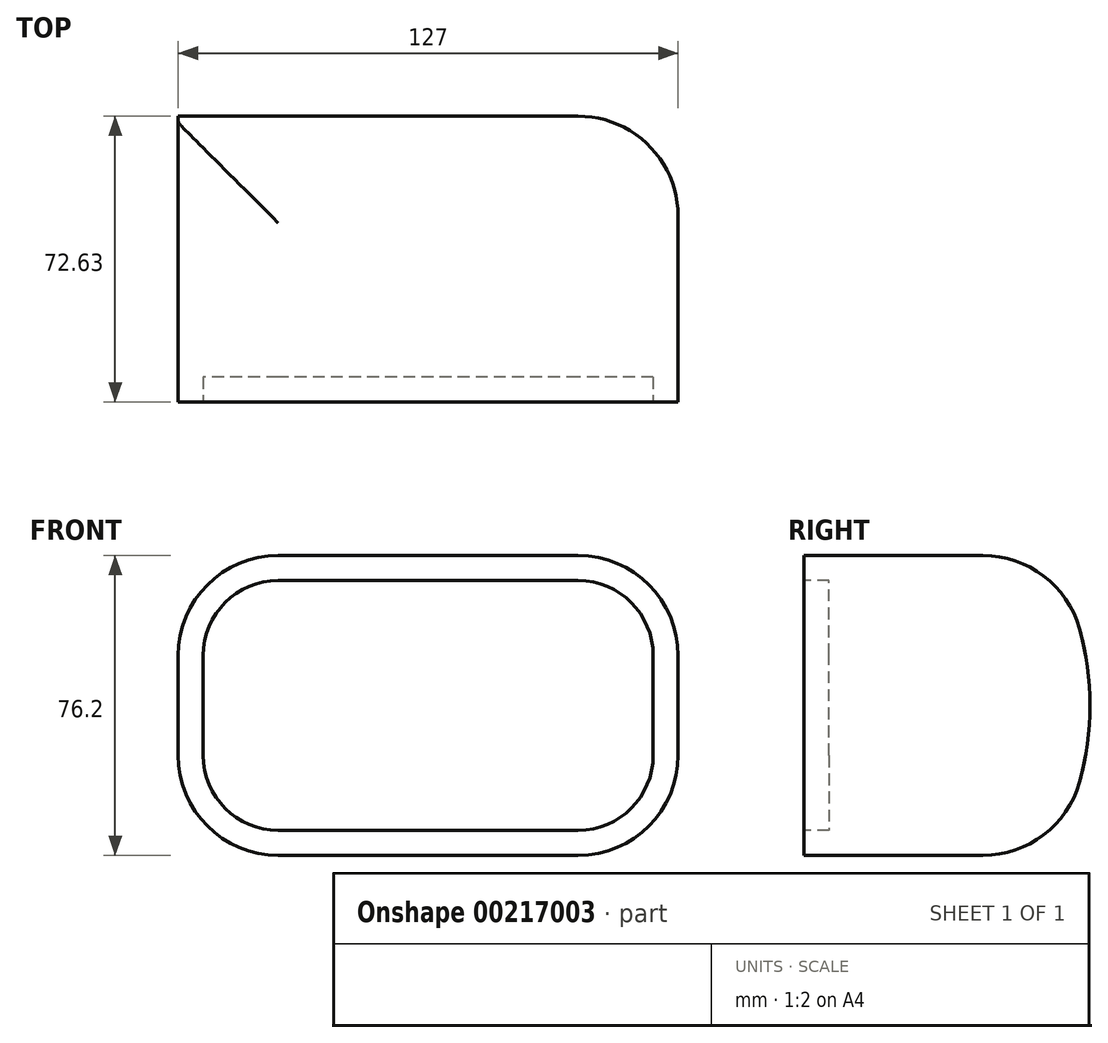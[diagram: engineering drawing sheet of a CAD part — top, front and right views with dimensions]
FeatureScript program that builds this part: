
annotation { "Feature Type Name" : "Feature", "Feature Type Description" : "" }
export const myFeature = defineFeature(function(context is Context, id is Id, definition is map)
    precondition{}
    {
        {
            var Q0;
            Q0=qCreatedBy(makeId("Front.planeOp"),FACE);
            var sketch = newSketch(context, id + "F0", { "sketchPlane" : qUnion([Q0])});
            skLineSegment(sketch, "E0.bottom", {"start": v(63.5, -38.1) * mm, "end": v(-63.5, -38.1) * mm});
            skLineSegment(sketch, "E0.top", {"start": v(63.5, 38.1) * mm, "end": v(-63.5, 38.1) * mm});
            skLineSegment(sketch, "E0.left", {"start": v(63.5, -38.1) * mm, "end": v(63.5, 38.1) * mm});
            skLineSegment(sketch, "E0.right", {"start": v(-63.5, -38.1) * mm, "end": v(-63.5, 38.1) * mm});
            skPoint(sketch, "E0.middle", {"position": v(0, 0) * mm});
            skSolve(sketch);
        }
        {
            var Q0;
            Q0=makeQuery(id+"F0.imprint","IMPRINT",FACE,{"disambiguationData":[TD([[makeQuery(id+"F0.imprint","IMPRINT",EDGE,{"derivedFrom":sQuery(id+"F0.wireOp",EDGE,"E0.bottom")}),-1.0]])]});
            extrude(context, id + "F1", {"entities" : qUnion([Q0]), "depth" : 76.2 * mm});
        }
        {
            var Q0;
            Q0=makeQuery(id+"F1.opExtrude","SWEPT_FACE",FACE,{"disambiguationData":[OSD([sQuery(id+"F0.wireOp",EDGE,"E0.right")])]});
            var sketch = newSketch(context, id + "F2", { "sketchPlane" : qUnion([Q0])});
            skCircle(sketch, "E1", {"center": v(76.2, 0) * mm, "radius": 72.63 * mm});
            skLineSegment(sketch, "E2", {"start": v(68.95, 72.27) * mm, "end": v(-52.1, 60.12) * mm});
            skLineSegment(sketch, "E3", {"start": v(-52.1, 60.12) * mm, "end": v(-33.1, -48.53) * mm});
            skLineSegment(sketch, "E4", {"start": v(-33.1, -48.53) * mm, "end": v(71.98, -72.5) * mm});
            skSolve(sketch);
        }
        {
            var Q0;
            {var subQ6=sQuery(id+"F2.wireOp",EDGE,"E2");Q0=makeQuery(id+"F2.imprint","IMPRINT",FACE,{"disambiguationData":[TD([[makeQuery(id+"F2.imprint","IMPRINT",EDGE,{"derivedFrom":subQ6}),1.0]])]});}
            var Q1;
            {var subQ1=sQuery(id+"F0.wireOp",EDGE,"E0.right");var subQ6=makeQuery(id+"F1.opExtrude","CAP_EDGE",EDGE,{"disambiguationData":[OSD([subQ1])],"isStart":true});Q1=makeQuery(id+"F2.imprint","IMPRINT",FACE,{"disambiguationData":[TD([[makeQuery(id+"F2.imprint","IMPRINT",EDGE,{"derivedFrom":subQ6}),-1.0]])]});}
            extrude(context, id + "F3", {"entities" : qUnion([Q0, Q1]), "operationType" : NewBodyOperationType.REMOVE, "endBound" : BoundingType.THROUGH_ALL, "oppositeDirection" : true, "depth" : 25.4 * mm});
        }
        {
            var Q0;
            Q0=makeQuery(id+"F1.opExtrude","SWEPT_EDGE",EDGE,{"disambiguationData":[OSD([sQuery(id+"F0.wireOp",EDGE,"E0.top"),sQuery(id+"F0.wireOp",EDGE,"E0.right")])]});
            var Q1;
            Q1=makeQuery(id+"F1.opExtrude","SWEPT_EDGE",EDGE,{"disambiguationData":[OSD([sQuery(id+"F0.wireOp",EDGE,"E0.top"),sQuery(id+"F0.wireOp",EDGE,"E0.left")])]});
            var Q2;
            Q2=makeQuery(id+"F1.opExtrude","SWEPT_EDGE",EDGE,{"disambiguationData":[OSD([sQuery(id+"F0.wireOp",EDGE,"E0.bottom"),sQuery(id+"F0.wireOp",EDGE,"E0.right")])]});
            var Q3;
            Q3=makeQuery(id+"F1.opExtrude","SWEPT_EDGE",EDGE,{"disambiguationData":[OSD([sQuery(id+"F0.wireOp",EDGE,"E0.bottom"),sQuery(id+"F0.wireOp",EDGE,"E0.left")])]});
            var Q4;
            Q4=makeQuery(id+"F3.boolean.opBoolean","INTERSECT",EDGE,{"derivedFrom":[makeQuery(id+"F1.opExtrude","SWEPT_FACE",FACE,{"disambiguationData":[OSD([sQuery(id+"F0.wireOp",EDGE,"E0.left")])]}),makeQuery(id+"F3.opExtrude","SWEPT_FACE",FACE,{"disambiguationData":[OSD([sQuery(id+"F2.wireOp",EDGE,"E1")])]})]});
            var Q5;
            Q5=makeQuery(id+"F3.boolean.opBoolean","COPY",EDGE,{"derivedFrom":makeQuery(id+"F3.opExtrude","CAP_EDGE",EDGE,{"disambiguationData":[OSD([sQuery(id+"F2.wireOp",EDGE,"E1")])],"isStart":true})});
            var Q6;
            Q6=makeQuery(id+"F3.boolean.opBoolean","INTERSECT",EDGE,{"derivedFrom":[makeQuery(id+"F1.opExtrude","SWEPT_FACE",FACE,{"disambiguationData":[OSD([sQuery(id+"F0.wireOp",EDGE,"E0.bottom")])]}),makeQuery(id+"F3.opExtrude","SWEPT_FACE",FACE,{"disambiguationData":[OSD([sQuery(id+"F2.wireOp",EDGE,"E1")])]})]});
            var Q7;
            Q7=makeQuery(id+"F3.boolean.opBoolean","INTERSECT",EDGE,{"derivedFrom":[makeQuery(id+"F1.opExtrude","SWEPT_FACE",FACE,{"disambiguationData":[OSD([sQuery(id+"F0.wireOp",EDGE,"E0.top")])]}),makeQuery(id+"F3.opExtrude","SWEPT_FACE",FACE,{"disambiguationData":[OSD([sQuery(id+"F2.wireOp",EDGE,"E1")])]})]});
            fillet(context, id + "F4", {"entities" : qUnion([Q0, Q1, Q2, Q3, Q4, Q5, Q6, Q7]), "radius" : 25.4 * mm, "tangentPropagation" : true, "allowEdgeOverflow" : false});
        }
        {
            var Q0;
            Q0=makeQuery(id+"F1.opExtrude","CAP_FACE",FACE,{"disambiguationData":[OSD([sQuery(id+"F0.wireOp",EDGE,"E0.bottom"),sQuery(id+"F0.wireOp",EDGE,"E0.top"),sQuery(id+"F0.wireOp",EDGE,"E0.left"),sQuery(id+"F0.wireOp",EDGE,"E0.right")])],"isStart":false});
            var sketch = newSketch(context, id + "F5", { "sketchPlane" : qUnion([Q0])});
            skArc(sketch, "E5.0", {"start": v(57.15, 12.7) * mm, "mid": v(51.57, 26.17) * mm, "end": v(38.1, 31.75) * mm});
            skLineSegment(sketch, "E5.1", {"start": v(57.15, -12.7) * mm, "end": v(57.15, 12.7) * mm});
            skLineSegment(sketch, "E5.2", {"start": v(38.1, 31.75) * mm, "end": v(-38.1, 31.75) * mm});
            skArc(sketch, "E5.3", {"start": v(38.1, -31.75) * mm, "mid": v(51.57, -26.17) * mm, "end": v(57.15, -12.7) * mm});
            skArc(sketch, "E5.4", {"start": v(-38.1, 31.75) * mm, "mid": v(-51.57, 26.17) * mm, "end": v(-57.15, 12.7) * mm});
            skLineSegment(sketch, "E5.5", {"start": v(-57.15, -12.7) * mm, "end": v(-57.15, 12.7) * mm});
            skArc(sketch, "E5.6", {"start": v(-57.15, -12.7) * mm, "mid": v(-51.57, -26.17) * mm, "end": v(-38.1, -31.75) * mm});
            skLineSegment(sketch, "E5.7", {"start": v(38.1, -31.75) * mm, "end": v(-38.1, -31.75) * mm});
            skSolve(sketch);
        }
        {
            var Q0;
            Q0=makeQuery(id+"F5.imprint","IMPRINT",FACE,{"disambiguationData":[TD([[makeQuery(id+"F5.imprint","IMPRINT",EDGE,{"derivedFrom":sQuery(id+"F5.wireOp",EDGE,"E5.0")}),1.0]])]});
            extrude(context, id + "F6", {"entities" : qUnion([Q0]), "operationType" : NewBodyOperationType.REMOVE, "oppositeDirection" : true, "depth" : 6.35 * mm});
        }
    });
